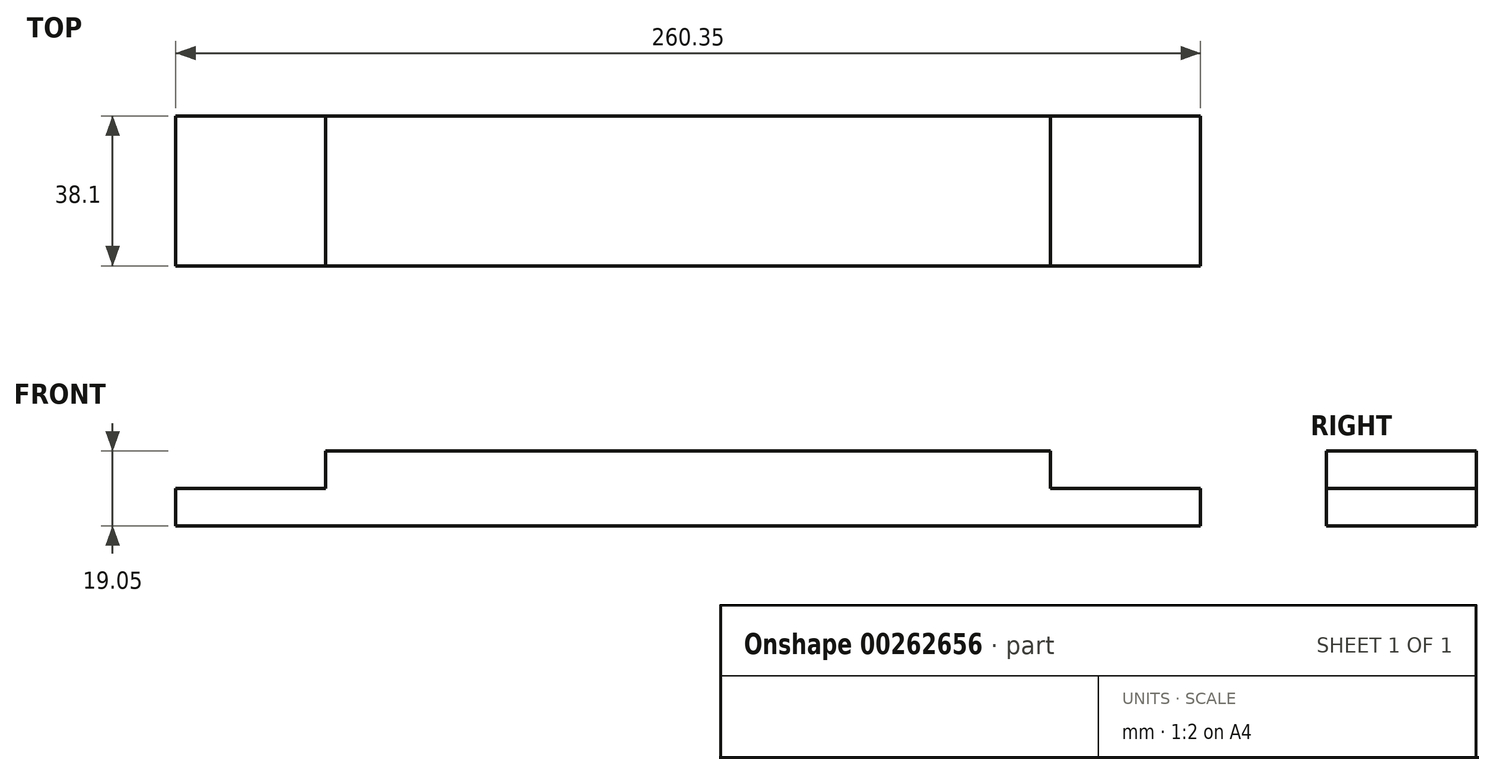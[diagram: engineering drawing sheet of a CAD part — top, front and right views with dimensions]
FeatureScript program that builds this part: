
annotation { "Feature Type Name" : "Feature", "Feature Type Description" : "" }
export const myFeature = defineFeature(function(context is Context, id is Id, definition is map)
    precondition{}
    {
        {
            var Q0;
            Q0=qCreatedBy(makeId("Front.planeOp"),FACE);
            var sketch = newSketch(context, id + "F0", { "sketchPlane" : qUnion([Q0])});
            skLineSegment(sketch, "E0", {"start": v(0, 0) * mm, "end": v(260.35, 0) * mm});
            skLineSegment(sketch, "E1", {"start": v(260.35, 9.53) * mm, "end": v(222.25, 9.52) * mm});
            skLineSegment(sketch, "E2", {"start": v(222.25, 9.52) * mm, "end": v(222.25, 19.05) * mm});
            skLineSegment(sketch, "E3", {"start": v(222.25, 19.05) * mm, "end": v(38.1, 19.05) * mm});
            skLineSegment(sketch, "E4", {"start": v(38.1, 19.05) * mm, "end": v(38.1, 9.53) * mm});
            skLineSegment(sketch, "E5", {"start": v(38.1, 9.53) * mm, "end": v(0, 9.52) * mm});
            skLineSegment(sketch, "E6", {"start": v(0, 9.52) * mm, "end": v(0, 0) * mm});
            skLineSegment(sketch, "E7", {"start": v(260.35, 9.53) * mm, "end": v(260.35, 0) * mm});
            skSolve(sketch);
        }
        {
            var Q0;
            Q0=makeQuery(id+"F0.imprint","IMPRINT",FACE,{"disambiguationData":[TD([[makeQuery(id+"F0.imprint","IMPRINT",EDGE,{"derivedFrom":sQuery(id+"F0.wireOp",EDGE,"E0")}),1.0]])]});
            extrude(context, id + "F1", {"entities" : qUnion([Q0]), "depth" : 38.1 * mm});
        }
    });
